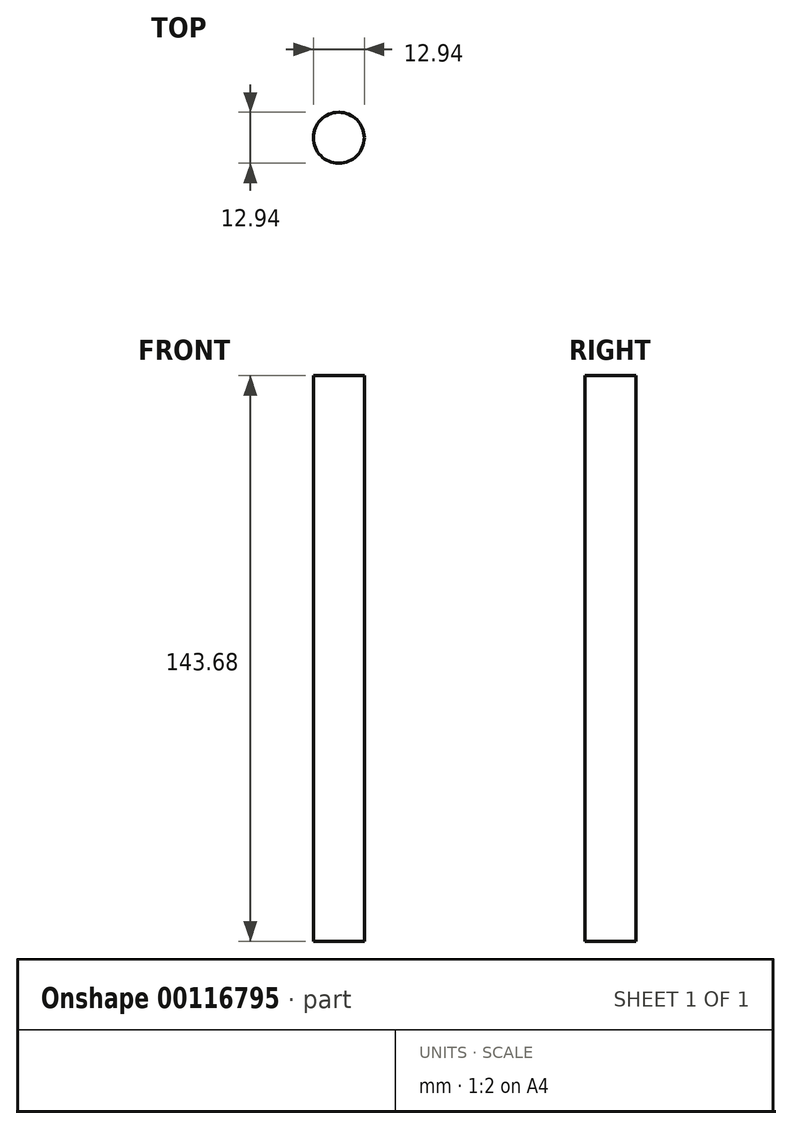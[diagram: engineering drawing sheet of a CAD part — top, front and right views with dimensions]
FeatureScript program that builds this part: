
annotation { "Feature Type Name" : "Feature", "Feature Type Description" : "" }
export const myFeature = defineFeature(function(context is Context, id is Id, definition is map)
    precondition{}
    {
        {
            var Q0;
            Q0=qCreatedBy(makeId("Top.planeOp"),FACE);
            var sketch = newSketch(context, id + "F0", { "sketchPlane" : qUnion([Q0])});
            skCircle(sketch, "E0", {"center": v(0, 0) * mm, "radius": 6.47 * mm});
            skSolve(sketch);
        }
        {
            var Q0;
            Q0=makeQuery(id+"F0.imprint","IMPRINT",FACE,{"disambiguationData":[TD([[makeQuery(id+"F0.imprint","IMPRINT",EDGE,{"derivedFrom":sQuery(id+"F0.wireOp",EDGE,"E0")}),1.0]])]});
            extrude(context, id + "F1", {"entities" : qUnion([Q0]), "depth" : 143.68 * mm});
        }
    });
